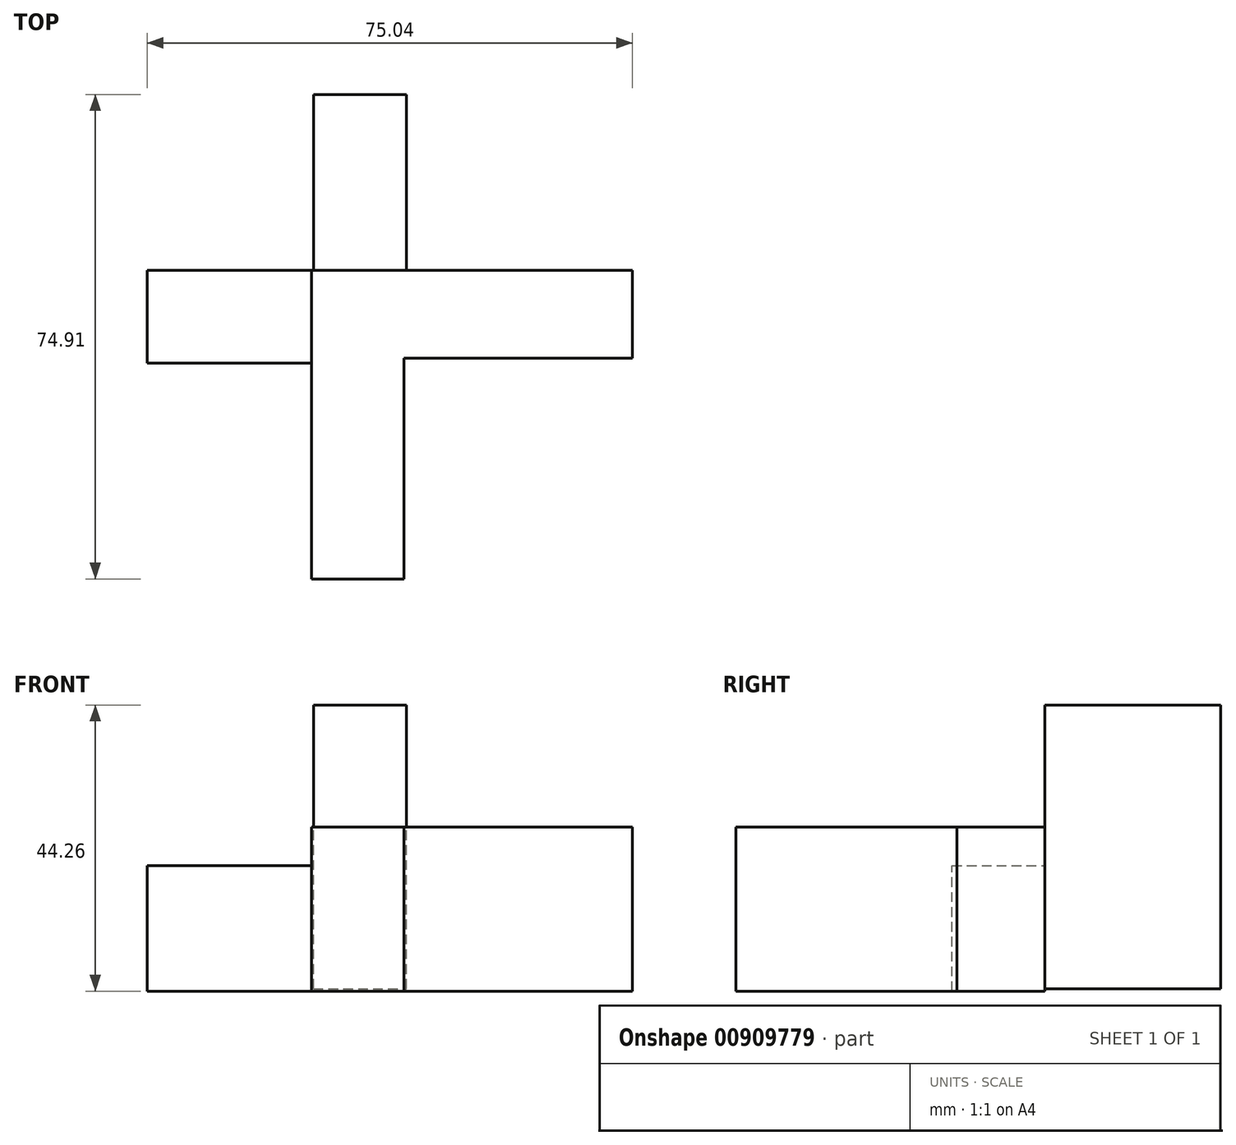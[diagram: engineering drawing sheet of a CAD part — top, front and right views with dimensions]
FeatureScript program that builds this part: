
annotation { "Feature Type Name" : "Feature", "Feature Type Description" : "" }
export const myFeature = defineFeature(function(context is Context, id is Id, definition is map)
    precondition{}
    {
        {
            var Q0;
            Q0=qCreatedBy(makeId("Top.planeOp"),FACE);
            var sketch = newSketch(context, id + "F0", { "sketchPlane" : qUnion([Q0])});
            skLineSegment(sketch, "E0.bottom", {"start": v(-20.75, -47.73) * mm, "end": v(-6.46, -47.73) * mm});
            skLineSegment(sketch, "E0.top", {"start": v(-20.75, 0) * mm, "end": v(-6.46, 0) * mm});
            skLineSegment(sketch, "E0.left", {"start": v(-20.75, -47.73) * mm, "end": v(-20.75, 0) * mm});
            skLineSegment(sketch, "E0.right", {"start": v(-6.46, -47.73) * mm, "end": v(-6.46, 0) * mm});
            skLineSegment(sketch, "E1.bottom", {"start": v(-20.75, 0) * mm, "end": v(28.9, 0) * mm});
            skLineSegment(sketch, "E1.top", {"start": v(-20.75, -13.6) * mm, "end": v(28.9, -13.6) * mm});
            skLineSegment(sketch, "E1.left", {"start": v(-20.75, 0) * mm, "end": v(-20.75, -13.6) * mm});
            skLineSegment(sketch, "E1.right", {"start": v(28.9, 0) * mm, "end": v(28.9, -13.6) * mm});
            skSolve(sketch);
        }
        {
            var Q0;
            Q0 = qSketchRegion(id + "F0", true);
            extrude(context, id + "F1", {"entities" : qUnion([Q0]), "endBound" : BoundingType.SYMMETRIC, "depth" : 25.4 * mm, "offsetDistance" : 25.4 * mm});
        }
        {
            var Q0;
            Q0=qCreatedBy(makeId("Front.planeOp"),FACE);
            var sketch = newSketch(context, id + "F2", { "sketchPlane" : qUnion([Q0])});
            skLineSegment(sketch, "E2.bottom", {"start": v(-20.41, -12.34) * mm, "end": v(-6.08, -12.34) * mm});
            skLineSegment(sketch, "E2.top", {"start": v(-20.41, 31.56) * mm, "end": v(-6.08, 31.56) * mm});
            skLineSegment(sketch, "E2.left", {"start": v(-20.41, -12.34) * mm, "end": v(-20.41, 31.56) * mm});
            skLineSegment(sketch, "E2.right", {"start": v(-6.08, -12.34) * mm, "end": v(-6.08, 31.56) * mm});
            skSolve(sketch);
        }
        {
            var Q0;
            Q0 = qSketchRegion(id + "F2", true);
            extrude(context, id + "F3", {"entities" : qUnion([Q0]), "operationType" : NewBodyOperationType.ADD, "oppositeDirection" : true, "depth" : 27.18 * mm, "offsetDistance" : 25.4 * mm});
        }
        {
            var Q0;
            Q0=makeQuery(id+"F1.opExtrude","SWEPT_FACE",FACE,{"disambiguationData":[OSD([sQuery(id+"F0.wireOp",EDGE,"E0.left"),sQuery(id+"F0.wireOp",EDGE,"E1.left")])]});
            var sketch = newSketch(context, id + "F4", { "sketchPlane" : qUnion([Q0])});
            skLineSegment(sketch, "E3.bottom", {"start": v(14.33, -12.7) * mm, "end": v(0, -12.7) * mm});
            skLineSegment(sketch, "E3.top", {"start": v(14.33, 6.7) * mm, "end": v(0, 6.7) * mm});
            skLineSegment(sketch, "E3.left", {"start": v(14.33, -12.7) * mm, "end": v(14.33, 6.7) * mm});
            skLineSegment(sketch, "E3.right", {"start": v(0, -12.7) * mm, "end": v(0, 6.7) * mm});
            skSolve(sketch);
        }
        {
            var Q0;
            Q0 = qSketchRegion(id + "F4", true);
            extrude(context, id + "F5", {"entities" : qUnion([Q0]), "operationType" : NewBodyOperationType.ADD, "depth" : 25.4 * mm, "offsetDistance" : 25.4 * mm});
        }
    });
